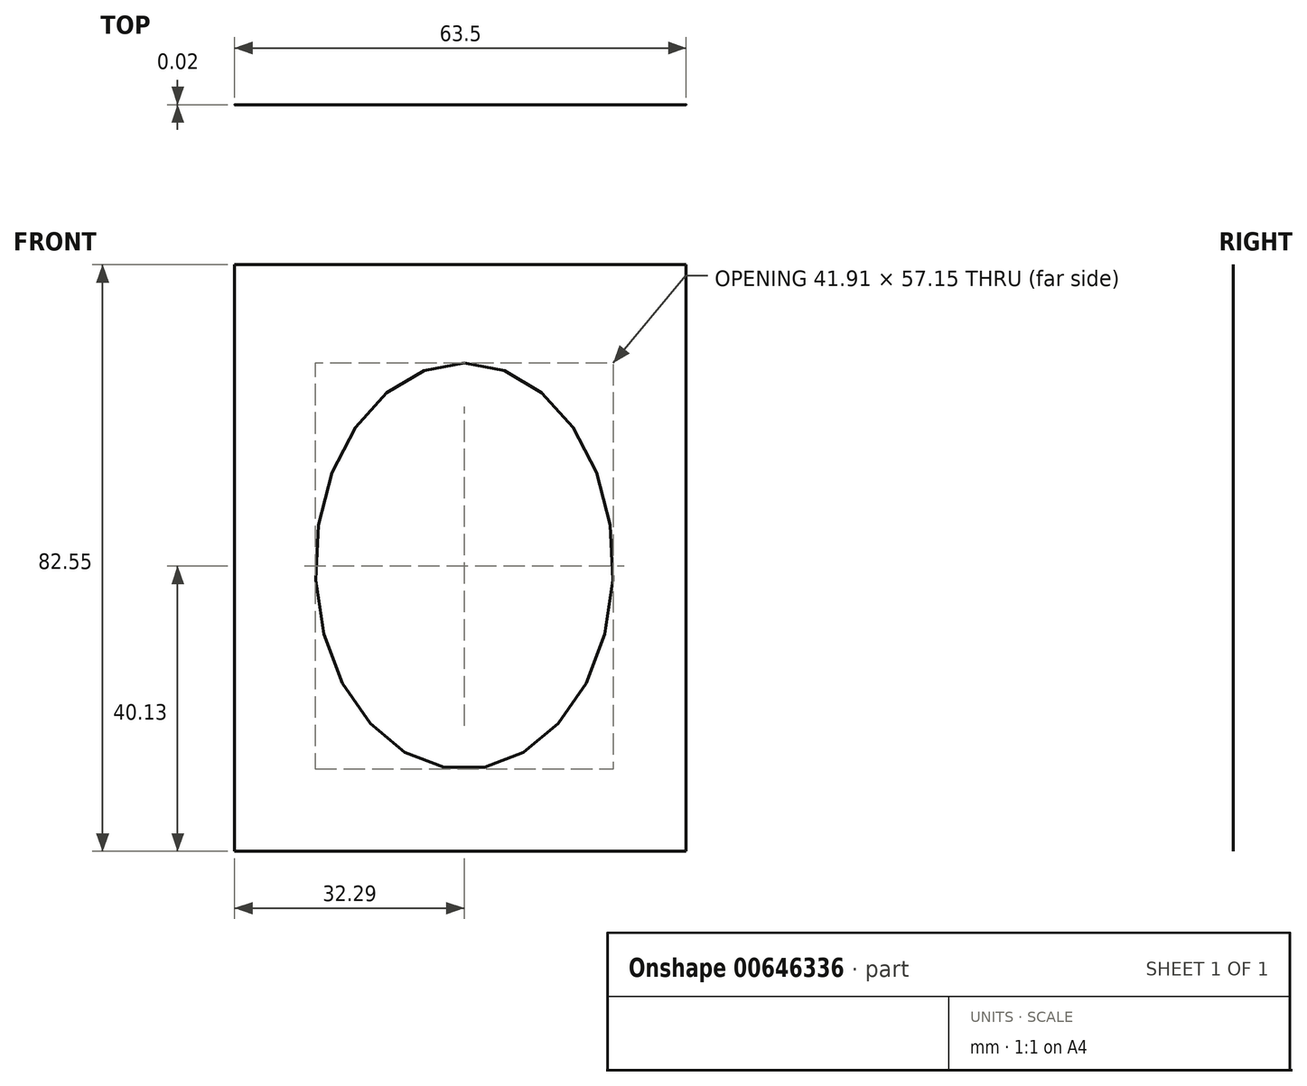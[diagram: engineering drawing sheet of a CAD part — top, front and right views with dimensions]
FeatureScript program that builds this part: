
annotation { "Feature Type Name" : "Feature", "Feature Type Description" : "" }
export const myFeature = defineFeature(function(context is Context, id is Id, definition is map)
    precondition{}
    {
        {
            var Q0;
            Q0=qCreatedBy(makeId("Front.planeOp"),FACE);
            var sketch = newSketch(context, id + "F0", { "sketchPlane" : qUnion([Q0])});
            skLineSegment(sketch, "E0.bottom", {"start": v(-32.29, 42.42) * mm, "end": v(31.21, 42.42) * mm});
            skLineSegment(sketch, "E0.top", {"start": v(-32.29, -40.13) * mm, "end": v(31.21, -40.13) * mm});
            skLineSegment(sketch, "E0.left", {"start": v(-32.29, 42.42) * mm, "end": v(-32.29, -40.13) * mm});
            skLineSegment(sketch, "E0.right", {"start": v(31.21, 42.42) * mm, "end": v(31.21, -40.13) * mm});
            skSolve(sketch);
        }
        {
            var Q0;
            Q0=makeQuery(id+"F0.imprint","IMPRINT",FACE,{"disambiguationData":[TD([[makeQuery(id+"F0.imprint","IMPRINT",EDGE,{"derivedFrom":sQuery(id+"F0.wireOp",EDGE,"E0.bottom")}),-1.0]])]});
            extrude(context, id + "F1", {"entities" : qUnion([Q0]), "depth" : 7 / 406.4 * mm, "offsetDistance" : 25.4 * mm});
        }
        {
            var Q0;
            Q0=makeQuery(id+"F1.opExtrude","SWEPT_FACE",FACE,{"disambiguationData":[OSD([sQuery(id+"F0.wireOp",EDGE,"E0.bottom")])]});
            var sketch = newSketch(context, id + "F2", { "sketchPlane" : qUnion([Q0])});
            skLineSegment(sketch, "E1.bottom", {"start": v(-31.21, -9.69) * mm, "end": v(29.78, -9.69) * mm});
            skLineSegment(sketch, "E1.top", {"start": v(-31.21, -5.41) * mm, "end": v(29.78, -5.41) * mm});
            skLineSegment(sketch, "E1.left", {"start": v(-31.21, -9.69) * mm, "end": v(-31.21, -5.41) * mm});
            skLineSegment(sketch, "E1.right", {"start": v(29.78, -9.69) * mm, "end": v(29.78, -5.41) * mm});
            skSolve(sketch);
        }
        {
            var Q0;
            Q0=makeQuery(id+"F2.imprint","IMPRINT",FACE,{"disambiguationData":[TD([[makeQuery(id+"F2.imprint","IMPRINT",EDGE,{"derivedFrom":sQuery(id+"F2.wireOp",EDGE,"E1.bottom")}),1.0]])]});
            extrude(context, id + "F3", {"entities" : qUnion([Q0]), "operationType" : NewBodyOperationType.REMOVE, "oppositeDirection" : true, "depth" : 63.5 * mm, "offsetDistance" : 25.4 * mm});
        }
        {
            var Q0;
            Q0=makeQuery(id+"F1.opExtrude","CAP_EDGE",EDGE,{"disambiguationData":[OSD([sQuery(id+"F0.wireOp",EDGE,"E0.bottom")])],"isStart":true});
            fillet(context, id + "F4", {"entities" : qUnion([Q0]), "radius" : 12.7 * mm, "tangentPropagation" : true, "allowEdgeOverflow" : false});
        }
        {
            var Q0;
            Q0=makeQuery(id+"F1.opExtrude","CAP_EDGE",EDGE,{"disambiguationData":[OSD([sQuery(id+"F0.wireOp",EDGE,"E0.top")])],"isStart":true});
            fillet(context, id + "F5", {"entities" : qUnion([Q0]), "radius" : 12.7 * mm, "tangentPropagation" : true, "allowEdgeOverflow" : false});
        }
        {
            var Q0;
            Q0=makeQuery(id+"F1.opExtrude","CAP_FACE",FACE,{"disambiguationData":[OSD([sQuery(id+"F0.wireOp",EDGE,"E0.bottom"),sQuery(id+"F0.wireOp",EDGE,"E0.top"),sQuery(id+"F0.wireOp",EDGE,"E0.left"),sQuery(id+"F0.wireOp",EDGE,"E0.right")])],"isStart":true});
            var sketch = newSketch(context, id + "F6", { "sketchPlane" : qUnion([Q0])});
            skEllipse(sketch, "E2", {"center": v(0, 0) * mm, "majorRadius": 28.58 * mm, "minorRadius": 20.96 * mm, "majorAxis": v(0, 1)});
            skSolve(sketch);
        }
        {
            var Q0;
            {var subQ0=sQuery(id+"F6.wireOp",EDGE,"E2");var subQ1=sQuery(id+"F0.wireOp",EDGE,"E0.top");var subQ2=makeQuery(id+"F5.opFillet","BLEND_EDGE",EDGE,{"blendedFrom":[makeQuery(id+"F1.opExtrude","CAP_EDGE",EDGE,{"disambiguationData":[OSD([subQ1])],"isStart":true}),makeQuery(id+"F1.opExtrude","CAP_FACE",FACE,{"disambiguationData":[OSD([sQuery(id+"F0.wireOp",EDGE,"E0.bottom"),subQ1,sQuery(id+"F0.wireOp",EDGE,"E0.left"),sQuery(id+"F0.wireOp",EDGE,"E0.right")])],"isStart":true})],"blendedInto":[makeQuery(id+"F1.opExtrude","CAP_FACE",FACE,{"disambiguationData":[OSD([sQuery(id+"F0.wireOp",EDGE,"E0.bottom"),subQ1,sQuery(id+"F0.wireOp",EDGE,"E0.left"),sQuery(id+"F0.wireOp",EDGE,"E0.right")])],"isStart":true})]});var subQ3=makeQuery(id+"F6.imprint","INTERSECT",VERTEX,{"disambiguationData":[OD(0.0)],"derivedFrom":[subQ2,subQ0]});Q0=makeQuery(id+"F6.imprint","IMPRINT",FACE,{"disambiguationData":[TD([[makeQuery(id+"F6.imprint","IMPRINT",EDGE,{"disambiguationData":[TD([[subQ3,-1.0]])],"derivedFrom":subQ0}),1.0]])]});}
            extrude(context, id + "F7", {"entities" : qUnion([Q0]), "operationType" : NewBodyOperationType.REMOVE, "oppositeDirection" : true, "depth" : 5.08 * mm, "offsetDistance" : 25.4 * mm});
        }
    });
